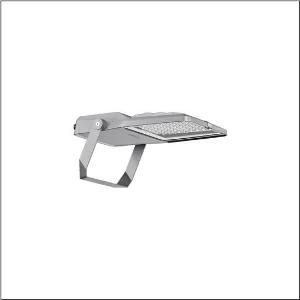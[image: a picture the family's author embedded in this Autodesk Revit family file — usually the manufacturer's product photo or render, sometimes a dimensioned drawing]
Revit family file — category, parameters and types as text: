
# Revit family: floodlight_fl_21_iq_mini___pl64_5xa7772b5e1a_cdb2
name_source: partatom
category: Lighting Fixtures
units: mm (PartAtom-declared; Revit-internal decimal feet)

## family parameters
Cut with Voids When Loaded = No
Host = Face
Light Source = No
Part Type = Normal
Room Calculation Point = No
Round Connector Dimension = Use Diameter
Shared = No

## types (1)
- --- (1 x LED, 5620 lm, 45.5 W, 4000K)
    Apparent Load = 46 VA
    CIE Flux Codes = 28 80 98 100 100
    Color Rendering = 80
    Color Temperature = 4000K
    Default Elevation = 1800 mm
    Description = Floodlight FL 21 iQ mini, floodlight, primary light control with lens, of PMMA, primary optical cover: protective disc, of toughened safety glass, transparent, light distribution: PL64, light emission: direct distribution, installation type: surface-mounted, lamps: LED, High Power LED, rated values: 5.620lm | 45,5W | 123,5lm/W (begin service life); end service life: 5.620lm | 48W; at 50% lumin. flux: 2.810lm | 21,5W | 130,7lm/W, colour temperature: 4000K, colour rendering: CRI > 80, light colour: 840, light setting 1 begin service life: 100% | 5.620lm | 45,5W | 123,5lm/W | 4.000K, light setting 1 end service life: 48W, further light settings possible, control: Street-Remote, Auto-Match, Temp-Guard, Night-Set, Smart-Wire, Desk-Remote (wireless, voltage-free reading and setting of iQ features in the workshop via application-optimized NFC function/RFID function), optimised constant luminous flux control (CLO 2.0), pre-setting: linear dimming characteristic, with terminal, 6-pole, mains connection: 220..240V, AC, 50/60Hz, luminaire housing, of diecast aluminium, powder-coated, SITECO metallic grey (DB 702S), corrosivity category C5 mid according to DIN EN ISO 12944suitable for swimming poolschlorine-resistant, sealing non-destructively replaceable, mounting bracket, of steel, galvanised, powder-coated, SITECO metallic grey (DB 702S), protection rating (complete): IP66, insulation class (complete): insulation class II (safety insulation), certification: CE, ENEC, VDE, protection symbol: D, impact resistance: IK08, permissible operating ambient temperature: -40..+40°C, permissible operating ambient temperature for outdoor applications: -40..+50°C, standard: DIN EN 12944, LABS conformity tested according to VDMA 24364:2018-05, packaging unit: 1 piece

Light Distribution: PL64
    Height = 70 mm
    Lamp = 1 x LED
    Lamp Light Flux = 5620 lm
    Lamp Power = 45.5 W
    Lamp count = 1
    Length = 485 mm
    Luminous efficacy = 124 lm/W
    Manufacturer = Siteco
    ModVariant = No
    Model = 5XA7772B5E1A
    Mounting Place = Pole
    Mounting Type = Pole annexe
    Number of Poles = 1
    OnlyDefault = Yes
    Power Factor = 1
    Product Name = Floodlight FL 21 iQ mini | PL64
    Product group = floodlight | pylon annexe
    ProductGroupID = 6201
    Protection Class = Protection class II
    Protection Degree = IP 66
    RLX_Detail_Level = 1
    RLX_Emergency_Light_Flux = 0 lm
    RLX_Emergency_Type = 0
    RLX_Emergency_Type_DB = No
    RlxData = <blob elided: 96369 chars, md5=4e71b365>
    Socket = socket
    Standby Power = 0 W
    System Light Flux = 5620 lm
    System Power = 46 W
    Type Comments = factory setting: luminous flux: 100 % | dim-lin: 254 | 463 mA
    Type Image = l_1006845.jpg
    URL = http://relux.com
    VarID = @adj_167755
    Voltage = 0 V
    Weight = 0.00 kg
    Width = 337 mm

## geometry (parser evidence)
native form markers: Blend x4, Sweep x13
no freeform markers — native parametric forms only
